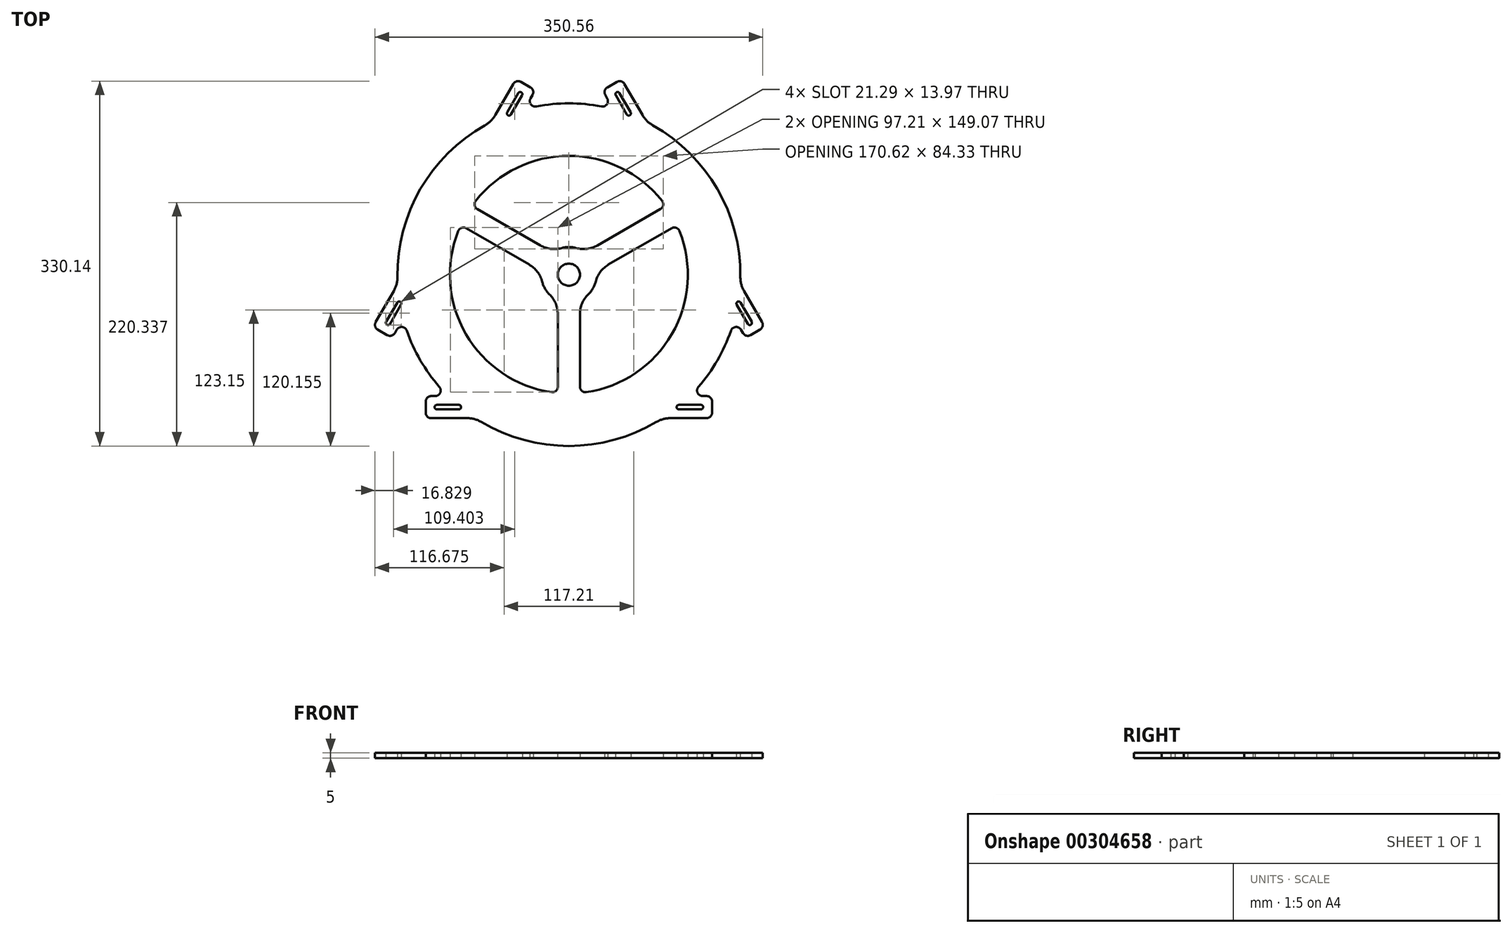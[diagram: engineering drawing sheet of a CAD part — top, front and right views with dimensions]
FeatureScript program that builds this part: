
annotation { "Feature Type Name" : "Feature", "Feature Type Description" : "" }
export const myFeature = defineFeature(function(context is Context, id is Id, definition is map)
    precondition{}
    {
        {
            var Q0;
            Q0=qCreatedBy(makeId("Top.planeOp"),FACE);
            var sketch = newSketch(context, id + "F0", { "sketchPlane" : qUnion([Q0])});
            skCircle(sketch, "E0", {"center": v(0, 0) * mm, "radius": 155 * mm});
            skCircle(sketch, "E1", {"center": v(0, 0) * mm, "radius": 150 * mm, "construction": true});
            skLineSegment(sketch, "E2.0", {"start": v(8.66, 244.6) * mm, "end": v(216.16, -114.8) * mm, "construction": true});
            skLineSegment(sketch, "E3.0", {"start": v(-216.16, -114.8) * mm, "end": v(-8.66, 244.6) * mm, "construction": true});
            skLineSegment(sketch, "E4.0", {"start": v(207.5, -129.8) * mm, "end": v(-207.5, -129.8) * mm, "construction": true});
            skLineSegment(sketch, "E5.0", {"start": v(207.5, -109.8) * mm, "end": v(-207.5, -109.8) * mm, "construction": true});
            skLineSegment(sketch, "E6.0", {"start": v(-198.84, -124.8) * mm, "end": v(8.66, 234.6) * mm, "construction": true});
            skLineSegment(sketch, "E7.0", {"start": v(-8.66, 234.6) * mm, "end": v(198.84, -124.8) * mm, "construction": true});
            skLineSegment(sketch, "E8", {"start": v(-40.39, 149.65) * mm, "end": v(-30.39, 166.97) * mm});
            skLineSegment(sketch, "E9", {"start": v(40.39, 149.65) * mm, "end": v(30.39, 166.97) * mm});
            skLineSegment(sketch, "E10", {"start": v(-149.8, -39.85) * mm, "end": v(-159.8, -57.17) * mm});
            skLineSegment(sketch, "E11", {"start": v(-109.4, -109.8) * mm, "end": v(-129.4, -109.8) * mm});
            skLineSegment(sketch, "E12", {"start": v(109.4, -109.8) * mm, "end": v(129.4, -109.8) * mm});
            skLineSegment(sketch, "E13", {"start": v(149.8, -39.85) * mm, "end": v(159.8, -57.17) * mm});
            skLineSegment(sketch, "E14", {"start": v(-30.39, 166.97) * mm, "end": v(-47.7, 176.97) * mm});
            skLineSegment(sketch, "E15", {"start": v(-47.7, 176.97) * mm, "end": v(-70.05, 138.27) * mm});
            skLineSegment(sketch, "E16", {"start": v(30.39, 166.97) * mm, "end": v(47.7, 176.97) * mm});
            skLineSegment(sketch, "E17", {"start": v(47.7, 176.97) * mm, "end": v(70.05, 138.27) * mm});
            skLineSegment(sketch, "E18", {"start": v(-159.8, -57.17) * mm, "end": v(-177.11, -47.17) * mm});
            skLineSegment(sketch, "E19", {"start": v(-177.11, -47.17) * mm, "end": v(-154.77, -8.47) * mm});
            skLineSegment(sketch, "E20", {"start": v(-129.4, -109.8) * mm, "end": v(-129.4, -129.8) * mm});
            skLineSegment(sketch, "E21", {"start": v(-129.4, -129.8) * mm, "end": v(-84.72, -129.8) * mm});
            skLineSegment(sketch, "E22", {"start": v(129.4, -109.8) * mm, "end": v(129.4, -129.8) * mm});
            skLineSegment(sketch, "E23", {"start": v(129.4, -129.8) * mm, "end": v(84.72, -129.8) * mm});
            skLineSegment(sketch, "E24", {"start": v(159.8, -57.17) * mm, "end": v(177.11, -47.17) * mm});
            skLineSegment(sketch, "E25", {"start": v(177.11, -47.17) * mm, "end": v(154.77, -8.47) * mm});
            skPoint(sketch, "E26", {"position": v(-39.05, 171.97) * mm});
            skPoint(sketch, "E27", {"position": v(39.05, 171.97) * mm});
            skPoint(sketch, "E28", {"position": v(-168.45, -52.17) * mm});
            skPoint(sketch, "E29", {"position": v(-129.4, -119.8) * mm});
            skPoint(sketch, "E30", {"position": v(129.4, -119.8) * mm});
            skPoint(sketch, "E31", {"position": v(168.45, -52.17) * mm});
            skLineSegment(sketch, "E32", {"start": v(-39.05, 171.97) * mm, "end": v(-44.05, 163.3) * mm, "construction": true});
            skLineSegment(sketch, "E33", {"start": v(-44.05, 163.3) * mm, "end": v(-54.05, 145.99) * mm, "construction": true});
            skLineSegment(sketch, "E34", {"start": v(39.05, 171.97) * mm, "end": v(44.05, 163.3) * mm, "construction": true});
            skLineSegment(sketch, "E35", {"start": v(44.05, 163.3) * mm, "end": v(54.05, 145.99) * mm, "construction": true});
            skLineSegment(sketch, "E36", {"start": v(-168.45, -52.17) * mm, "end": v(-163.45, -43.5) * mm, "construction": true});
            skLineSegment(sketch, "E37", {"start": v(-163.45, -43.5) * mm, "end": v(-153.45, -26.19) * mm, "construction": true});
            skLineSegment(sketch, "E38", {"start": v(-129.4, -119.8) * mm, "end": v(-119.4, -119.8) * mm, "construction": true});
            skLineSegment(sketch, "E39", {"start": v(-119.4, -119.8) * mm, "end": v(-99.4, -119.8) * mm, "construction": true});
            skLineSegment(sketch, "E40", {"start": v(129.4, -119.8) * mm, "end": v(119.4, -119.8) * mm, "construction": true});
            skLineSegment(sketch, "E41", {"start": v(119.4, -119.8) * mm, "end": v(99.4, -119.8) * mm, "construction": true});
            skLineSegment(sketch, "E42", {"start": v(168.45, -52.17) * mm, "end": v(163.45, -43.5) * mm, "construction": true});
            skLineSegment(sketch, "E43", {"start": v(163.45, -43.5) * mm, "end": v(153.45, -26.19) * mm, "construction": true});
            skCircle(sketch, "E44", {"center": v(-44.05, 163.3) * mm, "radius": 2 * mm});
            skCircle(sketch, "E45", {"center": v(-54.05, 145.99) * mm, "radius": 2 * mm});
            skCircle(sketch, "E46", {"center": v(54.05, 145.99) * mm, "radius": 2 * mm});
            skCircle(sketch, "E47", {"center": v(44.05, 163.3) * mm, "radius": 2 * mm});
            skCircle(sketch, "E48", {"center": v(-163.45, -43.5) * mm, "radius": 2 * mm});
            skCircle(sketch, "E49", {"center": v(-153.45, -26.19) * mm, "radius": 2 * mm});
            skCircle(sketch, "E50", {"center": v(-99.4, -119.8) * mm, "radius": 2 * mm});
            skCircle(sketch, "E51", {"center": v(-119.4, -119.8) * mm, "radius": 2 * mm});
            skCircle(sketch, "E52", {"center": v(99.4, -119.8) * mm, "radius": 2 * mm});
            skCircle(sketch, "E53", {"center": v(119.4, -119.8) * mm, "radius": 2 * mm});
            skCircle(sketch, "E54", {"center": v(153.45, -26.19) * mm, "radius": 2 * mm});
            skCircle(sketch, "E55", {"center": v(163.45, -43.5) * mm, "radius": 2 * mm});
            skLineSegment(sketch, "E56.0", {"start": v(119.4, -117.8) * mm, "end": v(99.4, -117.8) * mm});
            skLineSegment(sketch, "E57.0", {"start": v(119.4, -121.8) * mm, "end": v(99.4, -121.8) * mm});
            skLineSegment(sketch, "E58.0", {"start": v(161.72, -44.5) * mm, "end": v(151.72, -27.19) * mm});
            skLineSegment(sketch, "E59.0", {"start": v(165.18, -42.5) * mm, "end": v(155.18, -25.19) * mm});
            skLineSegment(sketch, "E60.0", {"start": v(-119.4, -121.8) * mm, "end": v(-99.4, -121.8) * mm});
            skLineSegment(sketch, "E61.0", {"start": v(-119.4, -117.8) * mm, "end": v(-99.4, -117.8) * mm});
            skLineSegment(sketch, "E62.0", {"start": v(-161.72, -44.5) * mm, "end": v(-151.72, -27.19) * mm});
            skLineSegment(sketch, "E63.0", {"start": v(-165.18, -42.5) * mm, "end": v(-155.18, -25.19) * mm});
            skLineSegment(sketch, "E64.0", {"start": v(-42.32, 162.3) * mm, "end": v(-52.32, 144.99) * mm});
            skLineSegment(sketch, "E65.0", {"start": v(-45.78, 164.3) * mm, "end": v(-55.78, 146.99) * mm});
            skLineSegment(sketch, "E66.0", {"start": v(45.78, 164.3) * mm, "end": v(55.78, 146.99) * mm});
            skLineSegment(sketch, "E67.0", {"start": v(42.32, 162.3) * mm, "end": v(52.32, 144.99) * mm});
            skCircle(sketch, "E68", {"center": v(0, 0) * mm, "radius": 10 * mm});
            skCircle(sketch, "E69", {"center": v(0, 0) * mm, "radius": 25 * mm});
            skLineSegment(sketch, "E70", {"start": v(0, 0) * mm, "end": v(95.09, 54.9) * mm, "construction": true});
            skLineSegment(sketch, "E71", {"start": v(0, 0) * mm, "end": v(0, -109.8) * mm, "construction": true});
            skLineSegment(sketch, "E72", {"start": v(0, 0) * mm, "end": v(-95.09, 54.9) * mm, "construction": true});
            skLineSegment(sketch, "E73", {"start": v(95.09, 54.9) * mm, "end": v(90.09, 63.56) * mm, "construction": true});
            skLineSegment(sketch, "E74", {"start": v(95.09, 54.9) * mm, "end": v(100.09, 46.24) * mm, "construction": true});
            skLineSegment(sketch, "E75", {"start": v(-95.09, 54.9) * mm, "end": v(-90.09, 63.56) * mm, "construction": true});
            skLineSegment(sketch, "E76", {"start": v(-95.09, 54.9) * mm, "end": v(-100.09, 46.24) * mm, "construction": true});
            skLineSegment(sketch, "E77", {"start": v(0, -109.8) * mm, "end": v(10, -109.8) * mm});
            skLineSegment(sketch, "E78", {"start": v(0, -109.8) * mm, "end": v(-10, -109.8) * mm, "construction": true});
            skLineSegment(sketch, "E79", {"start": v(-90.09, 63.56) * mm, "end": v(-100.09, 46.24) * mm});
            skLineSegment(sketch, "E80", {"start": v(90.09, 63.56) * mm, "end": v(100.09, 46.24) * mm});
            skLineSegment(sketch, "E81", {"start": v(10, -109.8) * mm, "end": v(-10, -109.8) * mm});
            skLineSegment(sketch, "E82", {"start": v(-100.09, 46.24) * mm, "end": v(-24.84, 2.8) * mm});
            skLineSegment(sketch, "E83", {"start": v(-90.09, 63.56) * mm, "end": v(-14.84, 20.12) * mm});
            skLineSegment(sketch, "E84", {"start": v(90.09, 63.56) * mm, "end": v(14.84, 20.12) * mm});
            skLineSegment(sketch, "E85", {"start": v(100.09, 46.24) * mm, "end": v(24.84, 2.8) * mm});
            skLineSegment(sketch, "E86", {"start": v(10, -109.8) * mm, "end": v(10, -22.91) * mm});
            skLineSegment(sketch, "E87", {"start": v(-10, -109.8) * mm, "end": v(-10, -22.91) * mm});
            skCircle(sketch, "E88", {"center": v(0, 0) * mm, "radius": 107.5 * mm});
            skSolve(sketch);
        }
        {
            var Q0;
            Q0 = qSketchRegion(id + "F0", true);
            var Q1;
            Q1=makeQuery(id+"F0.imprint","IMPRINT",FACE,{"disambiguationData":[TD([[makeQuery(id+"F0.imprint","IMPRINT",EDGE,{"derivedFrom":sQuery(id+"F0.wireOp",EDGE,"E79")}),1.0]])]});
            var Q2;
            Q2=makeQuery(id+"F0.imprint","IMPRINT",FACE,{"disambiguationData":[TD([[makeQuery(id+"F0.imprint","IMPRINT",EDGE,{"derivedFrom":sQuery(id+"F0.wireOp",EDGE,"E80")}),-1.0]])]});
            var Q3;
            {var subQ1=sQuery(id+"F0.wireOp",EDGE,"E81");var subQ5=makeQuery(id+"F0.imprint","IMPRINT",VERTEX,{"derivedFrom":subQ1});Q3=makeQuery(id+"F0.imprint","IMPRINT",FACE,{"disambiguationData":[TD([[makeQuery(id+"F0.imprint","IMPRINT",EDGE,{"disambiguationData":[TD([[subQ5,1.0]])],"derivedFrom":subQ1}),-1.0]])]});}
            var Q4;
            {var subQ0=sQuery(id+"F0.wireOp",EDGE,"E86");var subQ1=sQuery(id+"F0.wireOp",EDGE,"E69");var subQ2=makeQuery(id+"F0.imprint","INTERSECT",VERTEX,{"derivedFrom":[subQ1,subQ0]});Q4=makeQuery(id+"F0.imprint","IMPRINT",FACE,{"disambiguationData":[TD([[makeQuery(id+"F0.imprint","IMPRINT",EDGE,{"disambiguationData":[TD([[subQ2,1.0]])],"derivedFrom":subQ1}),-1.0]])]});}
            var Q5;
            {var subQ0=sQuery(id+"F0.wireOp",EDGE,"E82");var subQ1=sQuery(id+"F0.wireOp",EDGE,"E69");var subQ2=makeQuery(id+"F0.imprint","INTERSECT",VERTEX,{"derivedFrom":[subQ1,subQ0]});Q5=makeQuery(id+"F0.imprint","IMPRINT",FACE,{"disambiguationData":[TD([[makeQuery(id+"F0.imprint","IMPRINT",EDGE,{"disambiguationData":[TD([[subQ2,1.0]])],"derivedFrom":subQ1}),-1.0]])]});}
            var Q6;
            {var subQ0=sQuery(id+"F0.wireOp",EDGE,"E84");var subQ1=sQuery(id+"F0.wireOp",EDGE,"E69");var subQ2=makeQuery(id+"F0.imprint","INTERSECT",VERTEX,{"derivedFrom":[subQ1,subQ0]});Q6=makeQuery(id+"F0.imprint","IMPRINT",FACE,{"disambiguationData":[TD([[makeQuery(id+"F0.imprint","IMPRINT",EDGE,{"disambiguationData":[TD([[subQ2,1.0]])],"derivedFrom":subQ1}),-1.0]])]});}
            var Q7;
            Q7=makeQuery(id+"F0.imprint","IMPRINT",FACE,{"disambiguationData":[TD([[makeQuery(id+"F0.imprint","IMPRINT",EDGE,{"derivedFrom":sQuery(id+"F0.wireOp",EDGE,"E68")}),-1.0]])]});
            extrude(context, id + "F1", {"entities" : qUnion([Q0, Q1, Q2, Q3, Q4, Q5, Q6, Q7]), "depth" : 5 * mm});
        }
        {
            var Q0;
            Q0=makeQuery(id+"F1.opExtrude","SWEPT_EDGE",EDGE,{"disambiguationData":[OSD([sQuery(id+"F0.wireOp",EDGE,"E14"),sQuery(id+"F0.wireOp",EDGE,"E15")])]});
            var Q1;
            Q1=makeQuery(id+"F1.opExtrude","SWEPT_EDGE",EDGE,{"disambiguationData":[OSD([sQuery(id+"F0.wireOp",EDGE,"E8"),sQuery(id+"F0.wireOp",EDGE,"E14")])]});
            var Q2;
            Q2=makeQuery(id+"F1.opExtrude","SWEPT_EDGE",EDGE,{"disambiguationData":[OSD([sQuery(id+"F0.wireOp",EDGE,"E9"),sQuery(id+"F0.wireOp",EDGE,"E16")])]});
            var Q3;
            Q3=makeQuery(id+"F1.opExtrude","SWEPT_EDGE",EDGE,{"disambiguationData":[OSD([sQuery(id+"F0.wireOp",EDGE,"E16"),sQuery(id+"F0.wireOp",EDGE,"E17")])]});
            var Q4;
            Q4=makeQuery(id+"F1.opExtrude","SWEPT_EDGE",EDGE,{"disambiguationData":[OSD([sQuery(id+"F0.wireOp",EDGE,"E24"),sQuery(id+"F0.wireOp",EDGE,"E25")])]});
            var Q5;
            Q5=makeQuery(id+"F1.opExtrude","SWEPT_EDGE",EDGE,{"disambiguationData":[OSD([sQuery(id+"F0.wireOp",EDGE,"E18"),sQuery(id+"F0.wireOp",EDGE,"E19")])]});
            var Q6;
            Q6=makeQuery(id+"F1.opExtrude","SWEPT_EDGE",EDGE,{"disambiguationData":[OSD([sQuery(id+"F0.wireOp",EDGE,"E11"),sQuery(id+"F0.wireOp",EDGE,"E20")])]});
            var Q7;
            Q7=makeQuery(id+"F1.opExtrude","SWEPT_EDGE",EDGE,{"disambiguationData":[OSD([sQuery(id+"F0.wireOp",EDGE,"E12"),sQuery(id+"F0.wireOp",EDGE,"E22")])]});
            var Q8;
            Q8=makeQuery(id+"F1.opExtrude","SWEPT_EDGE",EDGE,{"disambiguationData":[OSD([sQuery(id+"F0.wireOp",EDGE,"E13"),sQuery(id+"F0.wireOp",EDGE,"E24")])]});
            var Q9;
            Q9=makeQuery(id+"F1.opExtrude","SWEPT_EDGE",EDGE,{"disambiguationData":[OSD([sQuery(id+"F0.wireOp",EDGE,"E22"),sQuery(id+"F0.wireOp",EDGE,"E23")])]});
            var Q10;
            Q10=makeQuery(id+"F1.opExtrude","SWEPT_EDGE",EDGE,{"disambiguationData":[OSD([sQuery(id+"F0.wireOp",EDGE,"E20"),sQuery(id+"F0.wireOp",EDGE,"E21")])]});
            var Q11;
            Q11=makeQuery(id+"F1.opExtrude","SWEPT_EDGE",EDGE,{"disambiguationData":[OSD([sQuery(id+"F0.wireOp",EDGE,"E10"),sQuery(id+"F0.wireOp",EDGE,"E18")])]});
            fillet(context, id + "F2", {"entities" : qUnion([Q0, Q1, Q2, Q3, Q4, Q5, Q6, Q7, Q8, Q9, Q10, Q11]), "radius" : 5 * mm, "tangentPropagation" : true, "allowEdgeOverflow" : false});
        }
        {
            var Q0;
            Q0=makeQuery(id+"F1.opExtrude","SWEPT_EDGE",EDGE,{"disambiguationData":[OSD([sQuery(id+"F0.wireOp",EDGE,"E0"),sQuery(id+"F0.wireOp",EDGE,"E10")])]});
            var Q1;
            Q1=makeQuery(id+"F1.opExtrude","SWEPT_EDGE",EDGE,{"disambiguationData":[OSD([sQuery(id+"F0.wireOp",EDGE,"E0"),sQuery(id+"F0.wireOp",EDGE,"E13")])]});
            var Q2;
            Q2=makeQuery(id+"F1.opExtrude","SWEPT_EDGE",EDGE,{"disambiguationData":[OSD([sQuery(id+"F0.wireOp",EDGE,"E0"),sQuery(id+"F0.wireOp",EDGE,"E9")])]});
            var Q3;
            Q3=makeQuery(id+"F1.opExtrude","SWEPT_EDGE",EDGE,{"disambiguationData":[OSD([sQuery(id+"F0.wireOp",EDGE,"E0"),sQuery(id+"F0.wireOp",EDGE,"E8")])]});
            var Q4;
            Q4=makeQuery(id+"F1.opExtrude","SWEPT_EDGE",EDGE,{"disambiguationData":[OSD([sQuery(id+"F0.wireOp",EDGE,"E0"),sQuery(id+"F0.wireOp",EDGE,"E11")])]});
            var Q5;
            Q5=makeQuery(id+"F1.opExtrude","SWEPT_EDGE",EDGE,{"disambiguationData":[OSD([sQuery(id+"F0.wireOp",EDGE,"E0"),sQuery(id+"F0.wireOp",EDGE,"E12")])]});
            fillet(context, id + "F3", {"entities" : qUnion([Q0, Q1, Q2, Q3, Q4, Q5]), "radius" : 5 * mm, "tangentPropagation" : true, "allowEdgeOverflow" : false});
        }
        {
            var Q0;
            Q0=makeQuery(id+"F1.opExtrude","SWEPT_EDGE",EDGE,{"disambiguationData":[OSD([sQuery(id+"F0.wireOp",EDGE,"E0"),sQuery(id+"F0.wireOp",EDGE,"E15")])]});
            var Q1;
            Q1=makeQuery(id+"F1.opExtrude","SWEPT_EDGE",EDGE,{"disambiguationData":[OSD([sQuery(id+"F0.wireOp",EDGE,"E0"),sQuery(id+"F0.wireOp",EDGE,"E19")])]});
            var Q2;
            Q2=makeQuery(id+"F1.opExtrude","SWEPT_EDGE",EDGE,{"disambiguationData":[OSD([sQuery(id+"F0.wireOp",EDGE,"E0"),sQuery(id+"F0.wireOp",EDGE,"E17")])]});
            var Q3;
            Q3=makeQuery(id+"F1.opExtrude","SWEPT_EDGE",EDGE,{"disambiguationData":[OSD([sQuery(id+"F0.wireOp",EDGE,"E0"),sQuery(id+"F0.wireOp",EDGE,"E25")])]});
            var Q4;
            Q4=makeQuery(id+"F1.opExtrude","SWEPT_EDGE",EDGE,{"disambiguationData":[OSD([sQuery(id+"F0.wireOp",EDGE,"E0"),sQuery(id+"F0.wireOp",EDGE,"E21")])]});
            var Q5;
            Q5=makeQuery(id+"F1.opExtrude","SWEPT_EDGE",EDGE,{"disambiguationData":[OSD([sQuery(id+"F0.wireOp",EDGE,"E0"),sQuery(id+"F0.wireOp",EDGE,"E23")])]});
            fillet(context, id + "F4", {"entities" : qUnion([Q0, Q1, Q2, Q3, Q4, Q5]), "radius" : 25 * mm, "tangentPropagation" : true, "allowEdgeOverflow" : false});
        }
        {
            var Q0;
            Q0=makeQuery(id+"F1.opExtrude","SWEPT_EDGE",EDGE,{"disambiguationData":[OSD([sQuery(id+"F0.wireOp",EDGE,"E69"),sQuery(id+"F0.wireOp",EDGE,"E87")])]});
            var Q1;
            Q1=makeQuery(id+"F1.opExtrude","SWEPT_EDGE",EDGE,{"disambiguationData":[OSD([sQuery(id+"F0.wireOp",EDGE,"E69"),sQuery(id+"F0.wireOp",EDGE,"E82")])]});
            var Q2;
            Q2=makeQuery(id+"F1.opExtrude","SWEPT_EDGE",EDGE,{"disambiguationData":[OSD([sQuery(id+"F0.wireOp",EDGE,"E69"),sQuery(id+"F0.wireOp",EDGE,"E86")])]});
            var Q3;
            Q3=makeQuery(id+"F1.opExtrude","SWEPT_EDGE",EDGE,{"disambiguationData":[OSD([sQuery(id+"F0.wireOp",EDGE,"E69"),sQuery(id+"F0.wireOp",EDGE,"E85")])]});
            var Q4;
            Q4=makeQuery(id+"F1.opExtrude","SWEPT_EDGE",EDGE,{"disambiguationData":[OSD([sQuery(id+"F0.wireOp",EDGE,"E69"),sQuery(id+"F0.wireOp",EDGE,"E84")])]});
            var Q5;
            Q5=makeQuery(id+"F1.opExtrude","SWEPT_EDGE",EDGE,{"disambiguationData":[OSD([sQuery(id+"F0.wireOp",EDGE,"E69"),sQuery(id+"F0.wireOp",EDGE,"E83")])]});
            fillet(context, id + "F5", {"entities" : qUnion([Q0, Q1, Q2, Q3, Q4, Q5]), "radius" : 25 * mm, "tangentPropagation" : true, "allowEdgeOverflow" : false});
        }
        {
            var Q0;
            Q0=makeQuery(id+"F1.opExtrude","SWEPT_EDGE",EDGE,{"disambiguationData":[OSD([sQuery(id+"F0.wireOp",EDGE,"E82"),sQuery(id+"F0.wireOp",EDGE,"E88")])]});
            var Q1;
            Q1=makeQuery(id+"F1.opExtrude","SWEPT_EDGE",EDGE,{"disambiguationData":[OSD([sQuery(id+"F0.wireOp",EDGE,"E85"),sQuery(id+"F0.wireOp",EDGE,"E88")])]});
            var Q2;
            Q2=makeQuery(id+"F1.opExtrude","SWEPT_EDGE",EDGE,{"disambiguationData":[OSD([sQuery(id+"F0.wireOp",EDGE,"E86"),sQuery(id+"F0.wireOp",EDGE,"E88")])]});
            var Q3;
            Q3=makeQuery(id+"F1.opExtrude","SWEPT_EDGE",EDGE,{"disambiguationData":[OSD([sQuery(id+"F0.wireOp",EDGE,"E83"),sQuery(id+"F0.wireOp",EDGE,"E88")])]});
            var Q4;
            Q4=makeQuery(id+"F1.opExtrude","SWEPT_EDGE",EDGE,{"disambiguationData":[OSD([sQuery(id+"F0.wireOp",EDGE,"E84"),sQuery(id+"F0.wireOp",EDGE,"E88")])]});
            var Q5;
            Q5=makeQuery(id+"F1.opExtrude","SWEPT_EDGE",EDGE,{"disambiguationData":[OSD([sQuery(id+"F0.wireOp",EDGE,"E87"),sQuery(id+"F0.wireOp",EDGE,"E88")])]});
            fillet(context, id + "F6", {"entities" : qUnion([Q0, Q1, Q2, Q3, Q4, Q5]), "radius" : 5 * mm, "tangentPropagation" : true, "allowEdgeOverflow" : false});
        }
    });
